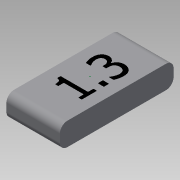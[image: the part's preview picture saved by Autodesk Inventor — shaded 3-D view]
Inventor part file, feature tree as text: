
AUTODESK INVENTOR PART (.ipt)
format: ipt  version: 2015 SP1 (Build 190203100, 203)  size: 83,456 bytes
history: native  units: mm
features: sketch x2, extrude x1, fillet x1
ambient origin geometry x8: Origin, YZ Plane, XZ Plane, XY Plane, X Axis, Y Axis, Z Axis, Center Point
bodies: Solid1 (feature_tree)
feature tree (4):
  extrude  "Extrusion1"  Depth=74.5mm
  fillet  "Fillet1"  Radius=15.0mm
  sketch  "Sketch2"  dims[d4=5.0mm]
  sketch  "Sketch1"  dims[d0=35.0mm d1=74.5mm d2=15.0mm d3=0.0mm]
